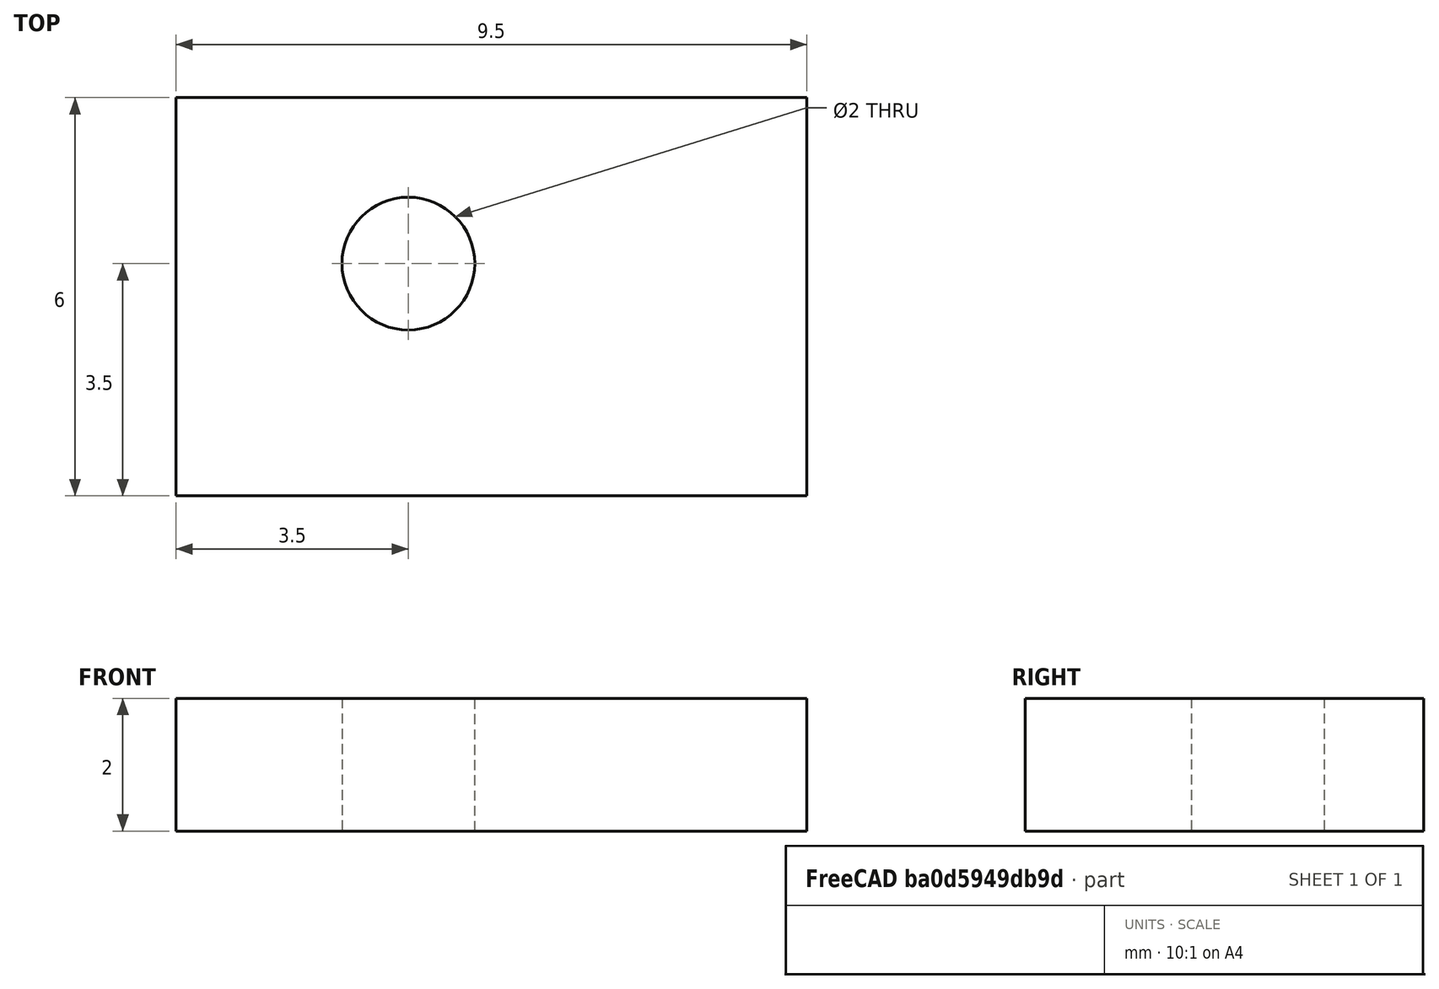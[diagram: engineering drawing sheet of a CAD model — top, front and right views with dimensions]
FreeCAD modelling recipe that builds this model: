
FCSTD DOCUMENT  (FreeCAD 1.0R39109 (Git))
Label: padding_for_ush_9.5x6x2
License: All rights reserved
LicenseURL: https://en.wikipedia.org/wiki/All_rights_reserved
objects: Sketcher::SketchObject×1, PartDesign::Pad×1, PartDesign::Body×1
note: 6 computed .brp shape members not serialized (recipe doc carries the construction recipe); baked Part::Feature solids carry a one-line shape summary decoded from their .brp

FEATURE [Sketcher::SketchObject] Sketch
  ArcFitTolerance = 1e-06
  AttachmentSupport = -> [XY_Plane]
  FullyConstrained = false
  MakeInternals = false
  MapMode = 5
  sketch-geometry (5):
    g0: LineSegment StartX=0 StartY=0 StartZ=0 EndX=9.5 EndY=0 EndZ=0
    g1: LineSegment StartX=9.5 StartY=0 StartZ=0 EndX=9.5 EndY=6 EndZ=0
    g2: LineSegment StartX=9.5 StartY=6 StartZ=0 EndX=0 EndY=6 EndZ=0
    g3: LineSegment StartX=0 StartY=6 StartZ=0 EndX=0 EndY=0 EndZ=0
    g4: Circle CenterX=3.49994 CenterY=3.49986 CenterZ=0 NormalX=0 NormalY=0 NormalZ=1 AngleXU=0 Radius=1
  constraints (12):
    c: Coincident(g0,g1)
    c: Coincident(g1,g2)
    c: Coincident(g2,g3)
    c: Coincident(g3,g0)
    c: Horizontal(g0)
    c: Horizontal(g2)
    c: Vertical(g1)
    c: Vertical(g3)
    c: Distance(g1,g3) = 9.5
    c: Distance(g0,g2) = 6
    c: Coincident(g0,g-1)
    c: Diameter(g4) = 2
FEATURE [PartDesign::Pad] Pad
  Direction = (0,0,1)
  Length = 2
  Length2 = 10
  Profile = -> Sketch
  ReferenceAxis = -> Sketch [N_Axis]
  Refine = true
  Suppressed = false
  Type = 0
FEATURE [PartDesign::Body] Body
  AllowCompound = false
  Group = -> [Sketch,Pad]
  Origin = -> Origin
  Tip = -> Pad
